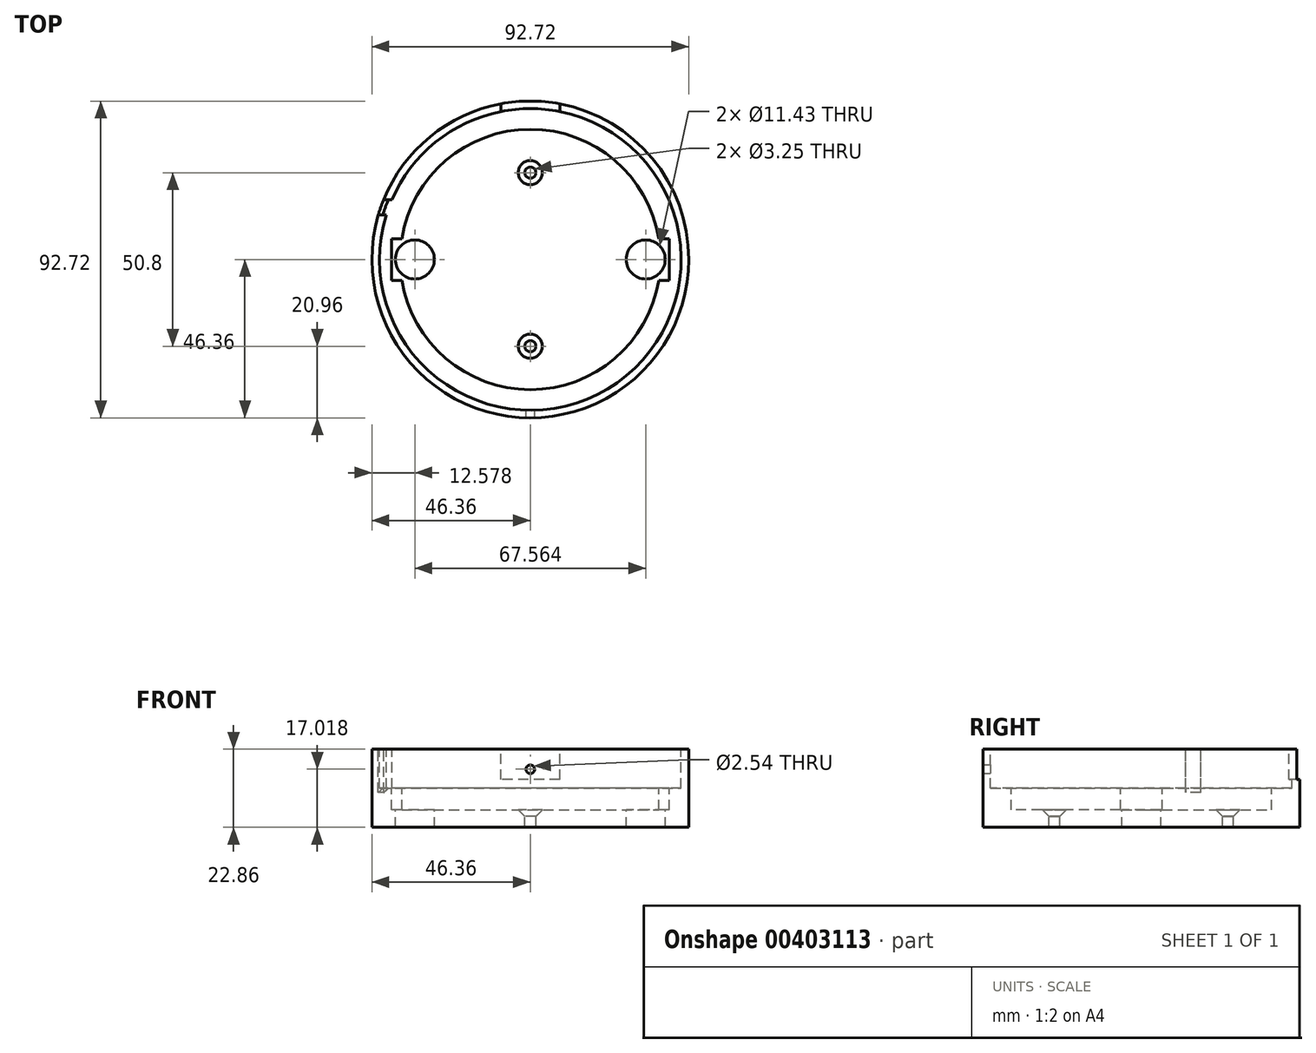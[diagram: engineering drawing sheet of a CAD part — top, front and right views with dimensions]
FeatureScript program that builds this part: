
annotation { "Feature Type Name" : "Feature", "Feature Type Description" : "" }
export const myFeature = defineFeature(function(context is Context, id is Id, definition is map)
    precondition{}
    {
        {
            var Q0;
            Q0=qCreatedBy(makeId("Top.planeOp"),FACE);
            var sketch = newSketch(context, id + "F0", { "sketchPlane" : qUnion([Q0])});
            skCircle(sketch, "E0", {"center": v(0, 0) * mm, "radius": 46.35 * mm});
            skSolve(sketch);
        }
        {
            var Q0;
            Q0 = qSketchRegion(id + "F0", true);
            extrude(context, id + "F1", {"entities" : qUnion([Q0]), "oppositeDirection" : true, "depth" : 22.86 * mm});
        }
        {
            var Q0;
            Q0=makeQuery(id+"F0.imprint","IMPRINT",FACE,{"disambiguationData":[TD([[makeQuery(id+"F0.imprint","IMPRINT",EDGE,{"derivedFrom":sQuery(id+"F0.wireOp",EDGE,"E0")}),1.0]])]});
            var sketch = newSketch(context, id + "F2", { "sketchPlane" : qUnion([Q0])});
            skCircle(sketch, "E1", {"center": v(0, 0) * mm, "radius": 44.13 * mm});
            skSolve(sketch);
        }
        {
            var Q0;
            Q0 = qSketchRegion(id + "F2", true);
            extrude(context, id + "F3", {"entities" : qUnion([Q0]), "operationType" : NewBodyOperationType.REMOVE, "oppositeDirection" : true, "depth" : 11.43 * mm});
        }
        {
            var Q0;
            Q0=qCreatedBy(makeId("Top.planeOp"),FACE);
            var sketch = newSketch(context, id + "F4", { "sketchPlane" : qUnion([Q0])});
            skCircle(sketch, "E2", {"center": v(0, 0) * mm, "radius": 38.1 * mm});
            skSolve(sketch);
        }
        {
            var Q0;
            Q0 = qSketchRegion(id + "F4", true);
            extrude(context, id + "F5", {"entities" : qUnion([Q0]), "operationType" : NewBodyOperationType.REMOVE, "oppositeDirection" : true, "depth" : 17.78 * mm});
        }
        {
            var Q0;
            Q0=qCreatedBy(makeId("Top.planeOp"),FACE);
            var sketch = newSketch(context, id + "F6", { "sketchPlane" : qUnion([Q0])});
            skLineSegment(sketch, "E3.bottom", {"start": v(40.64, -6.1) * mm, "end": v(-40.64, -6.1) * mm});
            skLineSegment(sketch, "E3.top", {"start": v(40.64, 6.1) * mm, "end": v(-40.64, 6.1) * mm});
            skLineSegment(sketch, "E3.left", {"start": v(40.64, -6.1) * mm, "end": v(40.64, 6.1) * mm});
            skLineSegment(sketch, "E3.right", {"start": v(-40.64, -6.1) * mm, "end": v(-40.64, 6.1) * mm});
            skPoint(sketch, "E3.middle", {"position": v(0, 0) * mm});
            skSolve(sketch);
        }
        {
            var Q0;
            Q0 = qSketchRegion(id + "F6", true);
            extrude(context, id + "F7", {"entities" : qUnion([Q0]), "operationType" : NewBodyOperationType.REMOVE, "oppositeDirection" : true, "depth" : 17.78 * mm});
        }
        {
            var Q0;
            Q0=qCreatedBy(makeId("Top.planeOp"),FACE);
            var sketch = newSketch(context, id + "F8", { "sketchPlane" : qUnion([Q0])});
            skCircle(sketch, "E4", {"center": v(-33.78, 0) * mm, "radius": 5.72 * mm});
            skCircle(sketch, "E5", {"center": v(33.78, 0) * mm, "radius": 5.72 * mm});
            skCircle(sketch, "E6", {"center": v(0, 0) * mm, "radius": 33.78 * mm, "construction": true});
            skSolve(sketch);
        }
        {
            var Q0;
            Q0 = qSketchRegion(id + "F8", true);
            extrude(context, id + "F9", {"entities" : qUnion([Q0]), "operationType" : NewBodyOperationType.REMOVE, "endBound" : BoundingType.THROUGH_ALL, "oppositeDirection" : true, "depth" : 25.4 * mm});
        }
        {
            var Q0;
            Q0=qCreatedBy(makeId("Front.planeOp"),FACE);
            var sketch = newSketch(context, id + "F10", { "sketchPlane" : qUnion([Q0])});
            skLineSegment(sketch, "E7", {"start": v(0, 11.43) * mm, "end": v(0, -41.9) * mm, "construction": true});
            skLineSegment(sketch, "E8", {"start": v(-13.1, -5.84) * mm, "end": v(22.62, -5.84) * mm, "construction": true});
            skCircle(sketch, "E9", {"center": v(0, -5.84) * mm, "radius": 1.27 * mm});
            skSolve(sketch);
        }
        {
            var Q0;
            Q0 = qSketchRegion(id + "F10", true);
            extrude(context, id + "F11", {"entities" : qUnion([Q0]), "operationType" : NewBodyOperationType.REMOVE, "endBound" : BoundingType.THROUGH_ALL, "depth" : 25.4 * mm});
        }
        {
            var Q0;
            Q0=qCreatedBy(makeId("Front.planeOp"),FACE);
            var sketch = newSketch(context, id + "F12", { "sketchPlane" : qUnion([Q0])});
            skLineSegment(sketch, "E10", {"start": v(0, 10.03) * mm, "end": v(0, -34.63) * mm, "construction": true});
            skLineSegment(sketch, "E11.bottom", {"start": v(8.64, 0) * mm, "end": v(-8.64, 0) * mm});
            skLineSegment(sketch, "E11.top", {"start": v(8.64, -8.89) * mm, "end": v(-8.64, -8.9) * mm});
            skLineSegment(sketch, "E11.left", {"start": v(8.64, 0) * mm, "end": v(8.64, -8.89) * mm});
            skLineSegment(sketch, "E11.right", {"start": v(-8.64, 0) * mm, "end": v(-8.64, -8.9) * mm});
            skPoint(sketch, "E11.middle", {"position": v(0, -4.45) * mm});
            skSolve(sketch);
        }
        {
            var Q0;
            Q0 = qSketchRegion(id + "F12", true);
            extrude(context, id + "F13", {"entities" : qUnion([Q0]), "operationType" : NewBodyOperationType.REMOVE, "endBound" : BoundingType.THROUGH_ALL, "oppositeDirection" : true, "depth" : 25.4 * mm});
        }
        {
            var Q0;
            Q0=qCreatedBy(makeId("Top.planeOp"),FACE);
            var sketch = newSketch(context, id + "F14", { "sketchPlane" : qUnion([Q0])});
            skLineSegment(sketch, "E12", {"start": v(0, 306.57) * mm, "end": v(0, -141.3) * mm, "construction": true});
            skLineSegment(sketch, "E13", {"start": v(-172.52, 0) * mm, "end": v(176.94, 0) * mm, "construction": true});
            skCircle(sketch, "E14", {"center": v(0, 25.4) * mm, "radius": 1.63 * mm});
            skCircle(sketch, "E15.MirrorC", {"center": v(0, -25.4) * mm, "radius": 1.63 * mm});
            skSolve(sketch);
        }
        {
            var Q0;
            Q0 = qSketchRegion(id + "F14", true);
            extrude(context, id + "F15", {"entities" : qUnion([Q0]), "operationType" : NewBodyOperationType.REMOVE, "endBound" : BoundingType.THROUGH_ALL, "oppositeDirection" : true, "depth" : 25.4 * mm});
        }
        {
            var Q0;
            Q0=makeQuery(id+"F15.boolean.opBoolean","INTERSECT",EDGE,{"derivedFrom":[makeQuery(id+"F7.boolean.opBoolean","MERGE",FACE,{"derivedFrom":[makeQuery(id+"F5.boolean.opBoolean","COPY",FACE,{"derivedFrom":makeQuery(id+"F5.opExtrude","CAP_FACE",FACE,{"disambiguationData":[OSD([sQuery(id+"F4.wireOp",EDGE,"E2")])],"isStart":false})}),makeQuery(id+"F7.opExtrude","CAP_FACE",FACE,{"disambiguationData":[OSD([sQuery(id+"F6.wireOp",EDGE,"E3.bottom"),sQuery(id+"F6.wireOp",EDGE,"E3.top"),sQuery(id+"F6.wireOp",EDGE,"E3.left"),sQuery(id+"F6.wireOp",EDGE,"E3.right")])],"isStart":false})]}),makeQuery(id+"F15.opExtrude","SWEPT_FACE",FACE,{"disambiguationData":[OSD([sQuery(id+"F14.wireOp",EDGE,"E14")])]})]});
            var Q1;
            Q1=makeQuery(id+"F15.boolean.opBoolean","INTERSECT",EDGE,{"derivedFrom":[makeQuery(id+"F7.boolean.opBoolean","MERGE",FACE,{"derivedFrom":[makeQuery(id+"F5.boolean.opBoolean","COPY",FACE,{"derivedFrom":makeQuery(id+"F5.opExtrude","CAP_FACE",FACE,{"disambiguationData":[OSD([sQuery(id+"F4.wireOp",EDGE,"E2")])],"isStart":false})}),makeQuery(id+"F7.opExtrude","CAP_FACE",FACE,{"disambiguationData":[OSD([sQuery(id+"F6.wireOp",EDGE,"E3.bottom"),sQuery(id+"F6.wireOp",EDGE,"E3.top"),sQuery(id+"F6.wireOp",EDGE,"E3.left"),sQuery(id+"F6.wireOp",EDGE,"E3.right")])],"isStart":false})]}),makeQuery(id+"F15.opExtrude","SWEPT_FACE",FACE,{"disambiguationData":[OSD([sQuery(id+"F14.wireOp",EDGE,"E15.MirrorC")])]})]});
            chamfer(context, id + "F16", {"entities" : qUnion([Q0, Q1]), "width" : 1.9 * mm, "tangentPropagation" : true});
        }
        {
            var Q0;
            Q0=qCreatedBy(makeId("Right.planeOp"),FACE);
            var sketch = newSketch(context, id + "F17", { "sketchPlane" : qUnion([Q0])});
            skLineSegment(sketch, "E16", {"start": v(15.24, 5.99) * mm, "end": v(15.24, -35.8) * mm, "construction": true});
            skLineSegment(sketch, "E17.bottom", {"start": v(17.46, 0) * mm, "end": v(13.02, 0) * mm});
            skLineSegment(sketch, "E17.top", {"start": v(17.46, -11.43) * mm, "end": v(13.02, -11.43) * mm});
            skLineSegment(sketch, "E17.left", {"start": v(17.46, 0) * mm, "end": v(17.46, -11.43) * mm});
            skLineSegment(sketch, "E17.right", {"start": v(13.02, 0) * mm, "end": v(13.02, -11.43) * mm});
            skPoint(sketch, "E17.middle", {"position": v(15.24, -5.72) * mm});
            skSolve(sketch);
        }
        {
            var Q0;
            Q0 = qSketchRegion(id + "F17", true);
            extrude(context, id + "F18", {"entities" : qUnion([Q0]), "operationType" : NewBodyOperationType.REMOVE, "endBound" : BoundingType.THROUGH_ALL, "oppositeDirection" : true, "depth" : 25.4 * mm});
        }
        {
            var Q0;
            Q0=makeQuery(id+"F18.boolean.opBoolean","INTERSECT",EDGE,{"derivedFrom":[makeQuery(id+"F1.opExtrude","SWEPT_FACE",FACE,{"disambiguationData":[OSD([sQuery(id+"F0.wireOp",EDGE,"E0")])]}),makeQuery(id+"F18.opExtrude","SWEPT_FACE",FACE,{"disambiguationData":[OSD([sQuery(id+"F17.wireOp",EDGE,"E17.top")])]})]});
            chamfer(context, id + "F19", {"entities" : qUnion([Q0]), "width" : 1.27 * mm, "tangentPropagation" : true});
        }
    });
